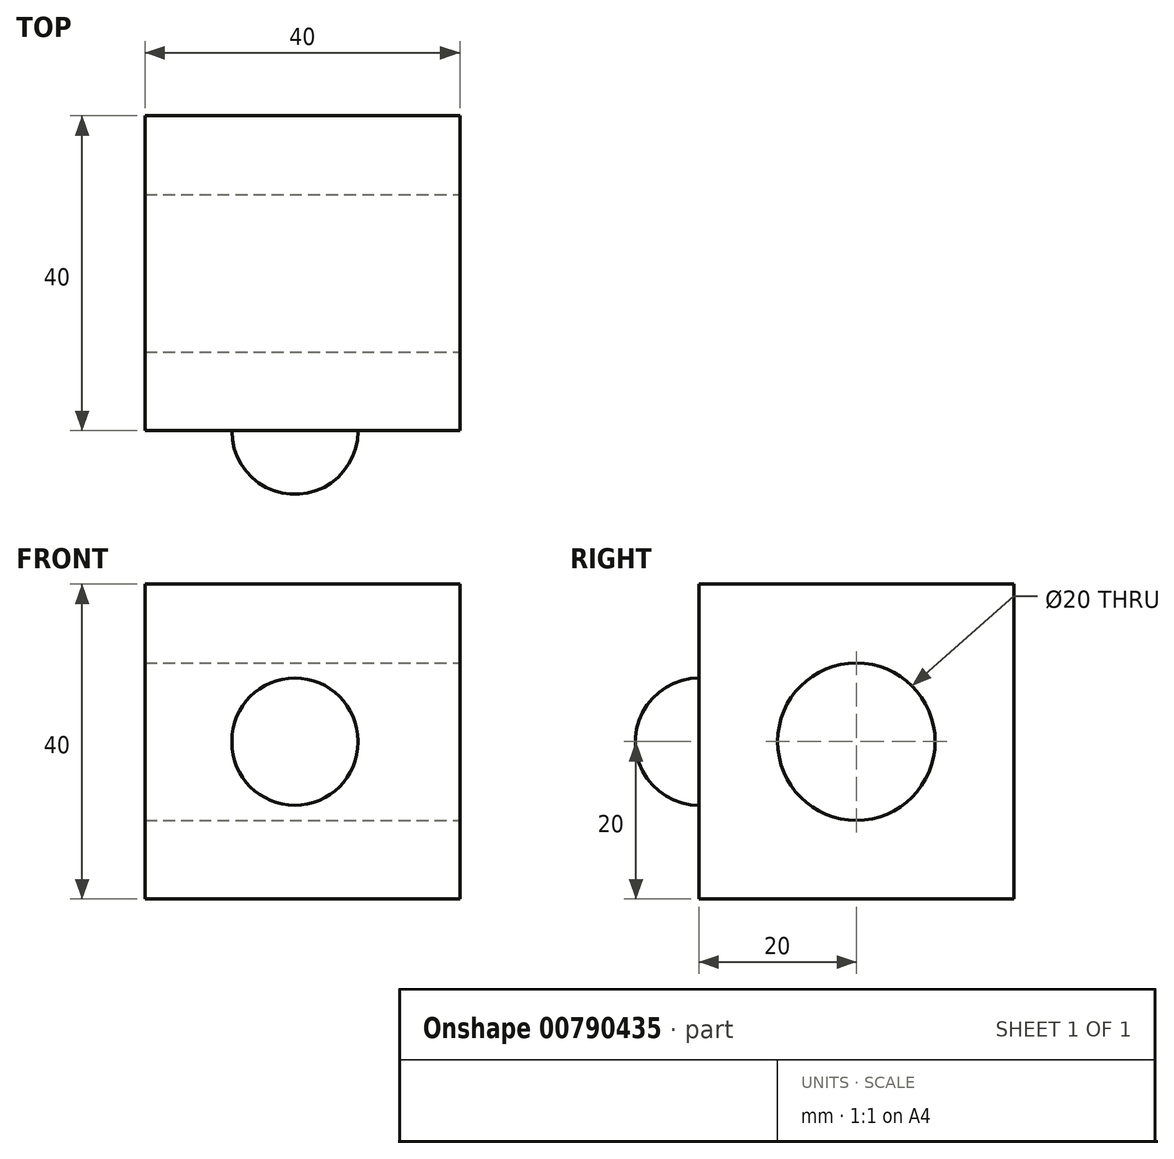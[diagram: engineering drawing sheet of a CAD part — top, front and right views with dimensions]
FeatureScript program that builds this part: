
annotation { "Feature Type Name" : "Feature", "Feature Type Description" : "" }
export const myFeature = defineFeature(function(context is Context, id is Id, definition is map)
    precondition{}
    {
        {
            var Q0;
            Q0=qCreatedBy(makeId("Front.planeOp"),FACE);
            var sketch = newSketch(context, id + "F0", { "sketchPlane" : qUnion([Q0])});
            skLineSegment(sketch, "E0.bottom", {"start": v(0, 0) * mm, "end": v(40, 0) * mm});
            skLineSegment(sketch, "E0.top", {"start": v(0, 40) * mm, "end": v(40, 40) * mm});
            skLineSegment(sketch, "E0.left", {"start": v(0, 0) * mm, "end": v(0, 40) * mm});
            skLineSegment(sketch, "E0.right", {"start": v(40, 0) * mm, "end": v(40, 40) * mm});
            skSolve(sketch);
        }
        {
            var Q0;
            Q0 = qSketchRegion(id + "F0", true);
            extrude(context, id + "F1", {"entities" : qUnion([Q0]), "depth" : 40 * mm, "offsetDistance" : 25 * mm});
        }
        {
            var Q0;
            Q0=makeQuery(id+"F1.opExtrude","SWEPT_FACE",FACE,{"disambiguationData":[OSD([sQuery(id+"F0.wireOp",EDGE,"E0.right")])]});
            var sketch = newSketch(context, id + "F2", { "sketchPlane" : qUnion([Q0])});
            skCircle(sketch, "E1", {"center": v(-20, 20) * mm, "radius": 10 * mm});
            skPoint(sketch, "E1.centerSnap0", {"position": v(-20, 40) * mm});
            skPoint(sketch, "E1.centerSnap1", {"position": v(-40, 20) * mm});
            skSolve(sketch);
        }
        {
            var Q0;
            Q0 = qSketchRegion(id + "F2", true);
            extrude(context, id + "F3", {"entities" : qUnion([Q0]), "operationType" : NewBodyOperationType.REMOVE, "endBound" : BoundingType.THROUGH_ALL, "oppositeDirection" : true, "depth" : 25 * mm, "offsetDistance" : 25 * mm});
        }
        {
            var Q0;
            Q0=makeQuery(id+"F1.opExtrude","CAP_FACE",FACE,{"disambiguationData":[OSD([sQuery(id+"F0.wireOp",EDGE,"E0.bottom"),sQuery(id+"F0.wireOp",EDGE,"E0.top"),sQuery(id+"F0.wireOp",EDGE,"E0.left"),sQuery(id+"F0.wireOp",EDGE,"E0.right")])],"isStart":false});
            var sketch = newSketch(context, id + "F4", { "sketchPlane" : qUnion([Q0])});
            skLineSegment(sketch, "E2", {"start": v(27.04, 20) * mm, "end": v(11.03, 20) * mm});
            skPoint(sketch, "E2.startSnap0", {"position": v(40, 20) * mm});
            skArc(sketch, "E3", {"start": v(11.03, 20) * mm, "mid": v(19.03, 11.92) * mm, "end": v(27.04, 20) * mm});
            skSolve(sketch);
        }
        {
            var Q0;
            Q0 = qSketchRegion(id + "F4", true);
            var Q1;
            Q1=sQuery(id+"F4.wireOp",EDGE,"E2");
            revolve(context, id + "F5", {"operationType" : NewBodyOperationType.ADD, "surfaceOperationType" : NewSurfaceOperationType.NEW, "entities" : qUnion([Q0]), "axis" : qUnion([Q1]), "revolveType" : RevolveType.FULL});
        }
    });
